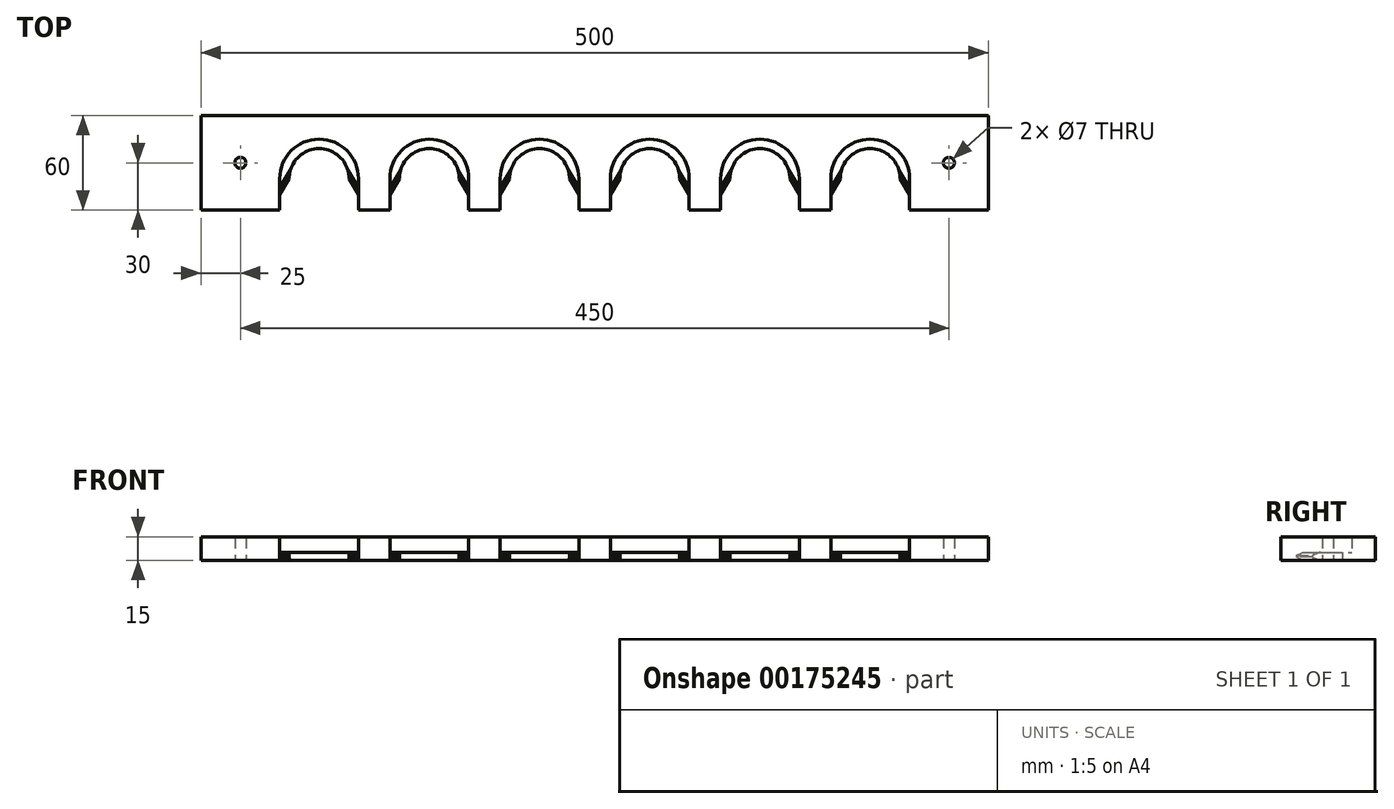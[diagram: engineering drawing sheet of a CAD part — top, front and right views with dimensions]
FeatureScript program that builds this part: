
annotation { "Feature Type Name" : "Feature", "Feature Type Description" : "" }
export const myFeature = defineFeature(function(context is Context, id is Id, definition is map)
    precondition{}
    {
        {
            var Q0;
            Q0=qCreatedBy(makeId("Top.planeOp"),FACE);
            var sketch = newSketch(context, id + "F0", { "sketchPlane" : qUnion([Q0])});
            skLineSegment(sketch, "E0.bottom", {"start": v(-250, -30) * mm, "end": v(250, -30) * mm});
            skLineSegment(sketch, "E0.top", {"start": v(-250, 30) * mm, "end": v(250, 30) * mm});
            skLineSegment(sketch, "E0.left", {"start": v(-250, -30) * mm, "end": v(-250, 30) * mm});
            skLineSegment(sketch, "E0.right", {"start": v(250, -30) * mm, "end": v(250, 30) * mm});
            skPoint(sketch, "E0.middle", {"position": v(0, 0) * mm});
            skLineSegment(sketch, "E1", {"start": v(-200, -30) * mm, "end": v(-200, -10) * mm});
            skArc(sketch, "E2", {"start": v(-150, -10) * mm, "mid": v(-175, 15) * mm, "end": v(-200, -10) * mm});
            skLineSegment(sketch, "E3", {"start": v(-150, -10) * mm, "end": v(-150, -30) * mm});
            skLineSegment(sketch, "E4", {"start": v(-200, -10) * mm, "end": v(-150, -10) * mm, "construction": true});
            skCircle(sketch, "E5", {"center": v(-225, 0) * mm, "radius": 3.5 * mm});
            skLineSegment(sketch, "E6", {"start": v(-250, 0) * mm, "end": v(-225, 0) * mm, "construction": true});
            skLineSegment(sketch, "E7", {"start": v(0, 0) * mm, "end": v(0, 30) * mm, "construction": true});
            skCircle(sketch, "E8.MirrorC", {"center": v(225, 0) * mm, "radius": 3.5 * mm});
            skLineSegment(sketch, "E9.1.0.0", {"start": v(-80, -10) * mm, "end": v(-80, -30) * mm});
            skArc(sketch, "E9.1.0.1", {"start": v(-80, -10) * mm, "mid": v(-105, 15) * mm, "end": v(-130, -10) * mm});
            skLineSegment(sketch, "E9.1.0.2", {"start": v(-130, -10) * mm, "end": v(-80, -10) * mm, "construction": true});
            skLineSegment(sketch, "E9.1.0.3", {"start": v(-130, -30) * mm, "end": v(-130, -10) * mm});
            skLineSegment(sketch, "E9.2.0.0", {"start": v(-10, -10) * mm, "end": v(-10, -30) * mm});
            skArc(sketch, "E9.2.0.1", {"start": v(-10, -10) * mm, "mid": v(-35, 15) * mm, "end": v(-60, -10) * mm});
            skLineSegment(sketch, "E9.2.0.2", {"start": v(-60, -10) * mm, "end": v(-10, -10) * mm, "construction": true});
            skLineSegment(sketch, "E9.2.0.3", {"start": v(-60, -30) * mm, "end": v(-60, -10) * mm});
            skLineSegment(sketch, "E9.3.0.0", {"start": v(60, -10) * mm, "end": v(60, -30) * mm});
            skArc(sketch, "E9.3.0.1", {"start": v(60, -10) * mm, "mid": v(35, 15) * mm, "end": v(10, -10) * mm});
            skLineSegment(sketch, "E9.3.0.2", {"start": v(10, -10) * mm, "end": v(60, -10) * mm, "construction": true});
            skLineSegment(sketch, "E9.3.0.3", {"start": v(10, -30) * mm, "end": v(10, -10) * mm});
            skLineSegment(sketch, "E9.4.0.0", {"start": v(130, -10) * mm, "end": v(130, -30) * mm});
            skArc(sketch, "E9.4.0.1", {"start": v(130, -10) * mm, "mid": v(105, 15) * mm, "end": v(80, -10) * mm});
            skLineSegment(sketch, "E9.4.0.2", {"start": v(80, -10) * mm, "end": v(130, -10) * mm, "construction": true});
            skLineSegment(sketch, "E9.4.0.3", {"start": v(80, -30) * mm, "end": v(80, -10) * mm});
            skLineSegment(sketch, "E9.5.0.0", {"start": v(200, -10) * mm, "end": v(200, -30) * mm});
            skArc(sketch, "E9.5.0.1", {"start": v(200, -10) * mm, "mid": v(175, 15) * mm, "end": v(150, -10) * mm});
            skLineSegment(sketch, "E9.5.0.2", {"start": v(150, -10) * mm, "end": v(200, -10) * mm, "construction": true});
            skLineSegment(sketch, "E9.5.0.3", {"start": v(150, -30) * mm, "end": v(150, -10) * mm});
            skLineSegment(sketch, "E9.direction1", {"start": v(-150, -30) * mm, "end": v(-80, -30) * mm, "construction": true});
            skSolve(sketch);
        }
        {
            var Q0;
            Q0=makeQuery(id+"F0.imprint","IMPRINT",FACE,{"disambiguationData":[TD([[makeQuery(id+"F0.imprint","IMPRINT",EDGE,{"derivedFrom":sQuery(id+"F0.wireOp",EDGE,"E0.top")}),-1.0]])]});
            extrude(context, id + "F1", {"entities" : qUnion([Q0]), "depth" : 15 * mm});
        }
        {
            var Q0;
            Q0=makeQuery(id+"F1.opExtrude","CAP_FACE",FACE,{"disambiguationData":[OSD([sQuery(id+"F0.wireOp",EDGE,"E0.bottom"),sQuery(id+"F0.wireOp",EDGE,"E0.top"),sQuery(id+"F0.wireOp",EDGE,"E0.left"),sQuery(id+"F0.wireOp",EDGE,"E0.right"),sQuery(id+"F0.wireOp",EDGE,"E1"),sQuery(id+"F0.wireOp",EDGE,"E2"),sQuery(id+"F0.wireOp",EDGE,"E3"),sQuery(id+"F0.wireOp",EDGE,"E5"),sQuery(id+"F0.wireOp",EDGE,"E8.MirrorC"),sQuery(id+"F0.wireOp",EDGE,"E9.1.0.0"),sQuery(id+"F0.wireOp",EDGE,"E9.1.0.1"),sQuery(id+"F0.wireOp",EDGE,"E9.1.0.3"),sQuery(id+"F0.wireOp",EDGE,"E9.2.0.0"),sQuery(id+"F0.wireOp",EDGE,"E9.2.0.1"),sQuery(id+"F0.wireOp",EDGE,"E9.2.0.3"),sQuery(id+"F0.wireOp",EDGE,"E9.3.0.0"),sQuery(id+"F0.wireOp",EDGE,"E9.3.0.1"),sQuery(id+"F0.wireOp",EDGE,"E9.3.0.3"),sQuery(id+"F0.wireOp",EDGE,"E9.4.0.0"),sQuery(id+"F0.wireOp",EDGE,"E9.4.0.1"),sQuery(id+"F0.wireOp",EDGE,"E9.4.0.3"),sQuery(id+"F0.wireOp",EDGE,"E9.5.0.0"),sQuery(id+"F0.wireOp",EDGE,"E9.5.0.1"),sQuery(id+"F0.wireOp",EDGE,"E9.5.0.3")])],"isStart":true});
            var sketch = newSketch(context, id + "F2", { "sketchPlane" : qUnion([Q0])});
            skLineSegment(sketch, "E10.1", {"start": v(-200, 10) * mm, "end": v(-200, 20) * mm});
            skArc(sketch, "E10.2", {"start": v(-150, 10) * mm, "mid": v(-175, -15) * mm, "end": v(-200, 10) * mm});
            skLineSegment(sketch, "E10.3", {"start": v(-150, 20) * mm, "end": v(-150, 10) * mm});
            skArc(sketch, "E11", {"start": v(-194, 10) * mm, "mid": v(-175, -9) * mm, "end": v(-156, 10) * mm});
            skLineSegment(sketch, "E12", {"start": v(-156, 10) * mm, "end": v(-150, 10) * mm, "construction": true});
            skLineSegment(sketch, "E13", {"start": v(-194, 10) * mm, "end": v(-200, 10) * mm, "construction": true});
            skLineSegment(sketch, "E14", {"start": v(-156, 10) * mm, "end": v(-150, 20) * mm});
            skLineSegment(sketch, "E15", {"start": v(-194, 10) * mm, "end": v(-200, 20) * mm});
            skArc(sketch, "E16.1.0.0", {"start": v(-124, 10) * mm, "mid": v(-105, -9) * mm, "end": v(-86, 10) * mm});
            skArc(sketch, "E16.1.0.1", {"start": v(-80, 10) * mm, "mid": v(-105, -15) * mm, "end": v(-130, 10) * mm});
            skLineSegment(sketch, "E16.1.0.2", {"start": v(-124, 10) * mm, "end": v(-130, 20) * mm});
            skLineSegment(sketch, "E16.1.0.3", {"start": v(-130, 10) * mm, "end": v(-130, 20) * mm});
            skLineSegment(sketch, "E16.1.0.4", {"start": v(-124, 10) * mm, "end": v(-130, 10) * mm, "construction": true});
            skLineSegment(sketch, "E16.1.0.5", {"start": v(-86, 10) * mm, "end": v(-80, 20) * mm});
            skLineSegment(sketch, "E16.1.0.6", {"start": v(-86, 10) * mm, "end": v(-80, 10) * mm, "construction": true});
            skLineSegment(sketch, "E16.1.0.7", {"start": v(-80, 20) * mm, "end": v(-80, 10) * mm});
            skLineSegment(sketch, "E16.1.0.8", {"start": v(-80, 20) * mm, "end": v(-80, 10) * mm});
            skLineSegment(sketch, "E16.1.0.9", {"start": v(-130, 10) * mm, "end": v(-130, 20) * mm});
            skArc(sketch, "E16.2.0.0", {"start": v(-54, 10) * mm, "mid": v(-35, -9) * mm, "end": v(-16, 10) * mm});
            skArc(sketch, "E16.2.0.1", {"start": v(-10, 10) * mm, "mid": v(-35, -15) * mm, "end": v(-60, 10) * mm});
            skLineSegment(sketch, "E16.2.0.2", {"start": v(-54, 10) * mm, "end": v(-60, 20) * mm});
            skLineSegment(sketch, "E16.2.0.3", {"start": v(-60, 10) * mm, "end": v(-60, 20) * mm});
            skLineSegment(sketch, "E16.2.0.4", {"start": v(-54, 10) * mm, "end": v(-60, 10) * mm, "construction": true});
            skLineSegment(sketch, "E16.2.0.5", {"start": v(-16, 10) * mm, "end": v(-10, 20) * mm});
            skLineSegment(sketch, "E16.2.0.6", {"start": v(-16, 10) * mm, "end": v(-10, 10) * mm, "construction": true});
            skLineSegment(sketch, "E16.2.0.7", {"start": v(-10, 20) * mm, "end": v(-10, 10) * mm});
            skLineSegment(sketch, "E16.2.0.8", {"start": v(-10, 20) * mm, "end": v(-10, 10) * mm});
            skLineSegment(sketch, "E16.2.0.9", {"start": v(-60, 10) * mm, "end": v(-60, 20) * mm});
            skArc(sketch, "E16.3.0.0", {"start": v(16, 10) * mm, "mid": v(35, -9) * mm, "end": v(54, 10) * mm});
            skArc(sketch, "E16.3.0.1", {"start": v(60, 10) * mm, "mid": v(35, -15) * mm, "end": v(10, 10) * mm});
            skLineSegment(sketch, "E16.3.0.2", {"start": v(16, 10) * mm, "end": v(10, 20) * mm});
            skLineSegment(sketch, "E16.3.0.3", {"start": v(10, 10) * mm, "end": v(10, 20) * mm});
            skLineSegment(sketch, "E16.3.0.4", {"start": v(16, 10) * mm, "end": v(10, 10) * mm, "construction": true});
            skLineSegment(sketch, "E16.3.0.5", {"start": v(54, 10) * mm, "end": v(60, 20) * mm});
            skLineSegment(sketch, "E16.3.0.6", {"start": v(54, 10) * mm, "end": v(60, 10) * mm, "construction": true});
            skLineSegment(sketch, "E16.3.0.7", {"start": v(60, 20) * mm, "end": v(60, 10) * mm});
            skLineSegment(sketch, "E16.3.0.8", {"start": v(60, 20) * mm, "end": v(60, 10) * mm});
            skLineSegment(sketch, "E16.3.0.9", {"start": v(10, 10) * mm, "end": v(10, 20) * mm});
            skArc(sketch, "E16.4.0.0", {"start": v(86, 10) * mm, "mid": v(105, -9) * mm, "end": v(124, 10) * mm});
            skArc(sketch, "E16.4.0.1", {"start": v(130, 10) * mm, "mid": v(105, -15) * mm, "end": v(80, 10) * mm});
            skLineSegment(sketch, "E16.4.0.2", {"start": v(86, 10) * mm, "end": v(80, 20) * mm});
            skLineSegment(sketch, "E16.4.0.3", {"start": v(80, 10) * mm, "end": v(80, 20) * mm});
            skLineSegment(sketch, "E16.4.0.4", {"start": v(86, 10) * mm, "end": v(80, 10) * mm, "construction": true});
            skLineSegment(sketch, "E16.4.0.5", {"start": v(124, 10) * mm, "end": v(130, 20) * mm});
            skLineSegment(sketch, "E16.4.0.6", {"start": v(124, 10) * mm, "end": v(130, 10) * mm, "construction": true});
            skLineSegment(sketch, "E16.4.0.7", {"start": v(130, 20) * mm, "end": v(130, 10) * mm});
            skLineSegment(sketch, "E16.4.0.8", {"start": v(130, 20) * mm, "end": v(130, 10) * mm});
            skLineSegment(sketch, "E16.4.0.9", {"start": v(80, 10) * mm, "end": v(80, 20) * mm});
            skArc(sketch, "E16.5.0.0", {"start": v(156, 10) * mm, "mid": v(175, -9) * mm, "end": v(194, 10) * mm});
            skArc(sketch, "E16.5.0.1", {"start": v(200, 10) * mm, "mid": v(175, -15) * mm, "end": v(150, 10) * mm});
            skLineSegment(sketch, "E16.5.0.2", {"start": v(156, 10) * mm, "end": v(150, 20) * mm});
            skLineSegment(sketch, "E16.5.0.3", {"start": v(150, 10) * mm, "end": v(150, 20) * mm});
            skLineSegment(sketch, "E16.5.0.4", {"start": v(156, 10) * mm, "end": v(150, 10) * mm, "construction": true});
            skLineSegment(sketch, "E16.5.0.5", {"start": v(194, 10) * mm, "end": v(200, 20) * mm});
            skLineSegment(sketch, "E16.5.0.6", {"start": v(194, 10) * mm, "end": v(200, 10) * mm, "construction": true});
            skLineSegment(sketch, "E16.5.0.7", {"start": v(200, 20) * mm, "end": v(200, 10) * mm});
            skLineSegment(sketch, "E16.5.0.8", {"start": v(200, 20) * mm, "end": v(200, 10) * mm});
            skLineSegment(sketch, "E16.5.0.9", {"start": v(150, 10) * mm, "end": v(150, 20) * mm});
            skLineSegment(sketch, "E16.direction1", {"start": v(-200, 10) * mm, "end": v(-130, 10) * mm, "construction": true});
            skSolve(sketch);
        }
        {
            var Q0;
            Q0 = qSketchRegion(id + "F2", true);
            extrude(context, id + "F3", {"entities" : qUnion([Q0]), "operationType" : NewBodyOperationType.ADD, "oppositeDirection" : true, "depth" : 5 * mm});
        }
        {
            var Q0;
            Q0=makeQuery(id+"F3.opExtrude","CAP_EDGE",EDGE,{"disambiguationData":[OSD([sQuery(id+"F2.wireOp",EDGE,"E15")])],"isStart":false});
            var Q1;
            Q1=makeQuery(id+"F3.opExtrude","CAP_EDGE",EDGE,{"disambiguationData":[OSD([sQuery(id+"F2.wireOp",EDGE,"E15")])],"isStart":true});
            var Q2;
            Q2=makeQuery(id+"F3.opExtrude","CAP_EDGE",EDGE,{"disambiguationData":[OSD([sQuery(id+"F2.wireOp",EDGE,"E16.2.0.2")])],"isStart":true});
            var Q3;
            Q3=makeQuery(id+"F3.opExtrude","CAP_EDGE",EDGE,{"disambiguationData":[OSD([sQuery(id+"F2.wireOp",EDGE,"E16.2.0.2")])],"isStart":false});
            var Q4;
            Q4=makeQuery(id+"F3.opExtrude","CAP_EDGE",EDGE,{"disambiguationData":[OSD([sQuery(id+"F2.wireOp",EDGE,"E16.1.0.2")])],"isStart":false});
            var Q5;
            Q5=makeQuery(id+"F3.opExtrude","CAP_EDGE",EDGE,{"disambiguationData":[OSD([sQuery(id+"F2.wireOp",EDGE,"E16.1.0.2")])],"isStart":true});
            var Q6;
            Q6=makeQuery(id+"F3.opExtrude","CAP_EDGE",EDGE,{"disambiguationData":[OSD([sQuery(id+"F2.wireOp",EDGE,"E14")])],"isStart":false});
            var Q7;
            Q7=makeQuery(id+"F3.opExtrude","CAP_EDGE",EDGE,{"disambiguationData":[OSD([sQuery(id+"F2.wireOp",EDGE,"E14")])],"isStart":true});
            var Q8;
            Q8=makeQuery(id+"F3.opExtrude","CAP_EDGE",EDGE,{"disambiguationData":[OSD([sQuery(id+"F2.wireOp",EDGE,"E16.1.0.5")])],"isStart":false});
            var Q9;
            Q9=makeQuery(id+"F3.opExtrude","CAP_EDGE",EDGE,{"disambiguationData":[OSD([sQuery(id+"F2.wireOp",EDGE,"E16.1.0.5")])],"isStart":true});
            var Q10;
            Q10=makeQuery(id+"F3.opExtrude","CAP_EDGE",EDGE,{"disambiguationData":[OSD([sQuery(id+"F2.wireOp",EDGE,"E16.2.0.5")])],"isStart":true});
            var Q11;
            Q11=makeQuery(id+"F3.opExtrude","CAP_EDGE",EDGE,{"disambiguationData":[OSD([sQuery(id+"F2.wireOp",EDGE,"E16.2.0.5")])],"isStart":false});
            var Q12;
            Q12=makeQuery(id+"F3.opExtrude","CAP_EDGE",EDGE,{"disambiguationData":[OSD([sQuery(id+"F2.wireOp",EDGE,"E16.3.0.5")])],"isStart":false});
            var Q13;
            Q13=makeQuery(id+"F3.opExtrude","CAP_EDGE",EDGE,{"disambiguationData":[OSD([sQuery(id+"F2.wireOp",EDGE,"E16.3.0.5")])],"isStart":true});
            var Q14;
            Q14=makeQuery(id+"F3.opExtrude","CAP_EDGE",EDGE,{"disambiguationData":[OSD([sQuery(id+"F2.wireOp",EDGE,"E16.4.0.5")])],"isStart":false});
            var Q15;
            Q15=makeQuery(id+"F3.opExtrude","CAP_EDGE",EDGE,{"disambiguationData":[OSD([sQuery(id+"F2.wireOp",EDGE,"E16.4.0.5")])],"isStart":true});
            var Q16;
            Q16=makeQuery(id+"F3.opExtrude","CAP_EDGE",EDGE,{"disambiguationData":[OSD([sQuery(id+"F2.wireOp",EDGE,"E16.5.0.5")])],"isStart":false});
            var Q17;
            Q17=makeQuery(id+"F3.opExtrude","CAP_EDGE",EDGE,{"disambiguationData":[OSD([sQuery(id+"F2.wireOp",EDGE,"E16.5.0.5")])],"isStart":true});
            var Q18;
            Q18=makeQuery(id+"F3.opExtrude","CAP_EDGE",EDGE,{"disambiguationData":[OSD([sQuery(id+"F2.wireOp",EDGE,"E16.3.0.2")])],"isStart":false});
            var Q19;
            Q19=makeQuery(id+"F3.opExtrude","CAP_EDGE",EDGE,{"disambiguationData":[OSD([sQuery(id+"F2.wireOp",EDGE,"E16.3.0.2")])],"isStart":true});
            var Q20;
            Q20=makeQuery(id+"F3.opExtrude","CAP_EDGE",EDGE,{"disambiguationData":[OSD([sQuery(id+"F2.wireOp",EDGE,"E16.4.0.2")])],"isStart":false});
            var Q21;
            Q21=makeQuery(id+"F3.opExtrude","CAP_EDGE",EDGE,{"disambiguationData":[OSD([sQuery(id+"F2.wireOp",EDGE,"E16.4.0.2")])],"isStart":true});
            var Q22;
            Q22=makeQuery(id+"F3.opExtrude","CAP_EDGE",EDGE,{"disambiguationData":[OSD([sQuery(id+"F2.wireOp",EDGE,"E16.5.0.2")])],"isStart":false});
            var Q23;
            Q23=makeQuery(id+"F3.opExtrude","CAP_EDGE",EDGE,{"disambiguationData":[OSD([sQuery(id+"F2.wireOp",EDGE,"E16.5.0.2")])],"isStart":true});
            chamfer(context, id + "F4", {"entities" : qUnion([Q0, Q1, Q2, Q3, Q4, Q5, Q6, Q7, Q8, Q9, Q10, Q11, Q12, Q13, Q14, Q15, Q16, Q17, Q18, Q19, Q20, Q21, Q22, Q23]), "width" : 2 * mm, "tangentPropagation" : true});
        }
    });
